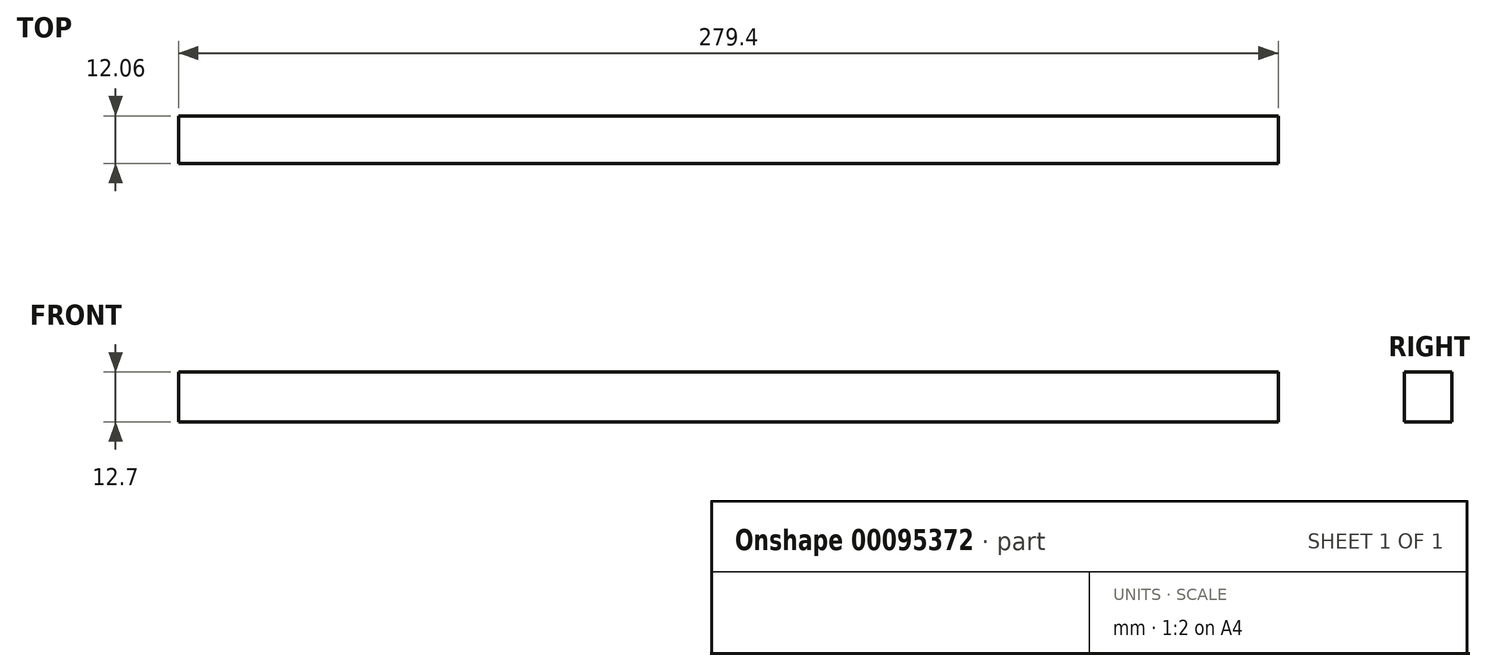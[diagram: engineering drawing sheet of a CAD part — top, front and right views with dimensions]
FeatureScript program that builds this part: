
annotation { "Feature Type Name" : "Feature", "Feature Type Description" : "" }
export const myFeature = defineFeature(function(context is Context, id is Id, definition is map)
    precondition{}
    {
        {
            var Q0;
            Q0=qCreatedBy(makeId("Top.planeOp"),FACE);
            var sketch = newSketch(context, id + "F0", { "sketchPlane" : qUnion([Q0])});
            skLineSegment(sketch, "E0.bottom", {"start": v(139.7, -6.03) * mm, "end": v(-139.7, -6.03) * mm});
            skLineSegment(sketch, "E0.top", {"start": v(139.7, 6.03) * mm, "end": v(-139.7, 6.03) * mm});
            skLineSegment(sketch, "E0.left", {"start": v(139.7, -6.03) * mm, "end": v(139.7, 6.03) * mm});
            skLineSegment(sketch, "E0.right", {"start": v(-139.7, -6.03) * mm, "end": v(-139.7, 6.03) * mm});
            skPoint(sketch, "E0.middle", {"position": v(0, 0) * mm});
            skSolve(sketch);
        }
        {
            var Q0;
            Q0 = qSketchRegion(id + "F0", true);
            extrude(context, id + "F1", {"entities" : qUnion([Q0]), "depth" : 12.7 * mm});
        }
    });
